# Revit family: НЕВАТОМ_Neiva 2 подвесная С-W-R 3000, Версия 2
name_source: partatom
category: Оборудование
revit_build: Autodesk Revit 2017 (Build: 20170118_1100(x64)
units: mm (PartAtom-declared; Revit-internal decimal feet)

## family parameters
Всегда вертикально = Нет
На основе рабочей плоскости = Да
Общий = Нет
При загрузке вырезать с полостями = Нет
Размер круглого соединителя = Использовать диаметр
Тип детали = Нормальный
Точка расчета площади = Нет

## types (1)
- C-3000-W-R
    A1 = 830 мм
    ADSK_Единица измерения = шт.
    ADSK_Завод-изготовитель = НЕВАТОМ
    ADSK_Количество = 1
    ADSK_Количество фаз = 3
    ADSK_Коэффициент мощности = 0.8
    ADSK_Марка = C-3000-W-R
    ADSK_Масса = 90
    ADSK_Материал наименование = сталь оцинкованная крашенная
    ADSK_Наименование = C-3000-W-R
    ADSK_Напряжение = 400 В
    ADSK_Номинальная мощность = 1140 Вт
    ADSK_Полная мощность = 1425 В·А
    ADSK_Потеря давления воздуха = 0.0 Па
    ADSK_Размер_Высота = 510 мм
    ADSK_Размер_Длина = 1218 мм
    ADSK_Размер_Ширина = 860 мм
    ADSK_Расход воздуха = 0.0 м³/ч
    ADSK_Температура воздуха на входе в нагреватель = 90 °C
    ADSK_Ток = 2 А
    Nevatom_Мощность нагревателя = 0 Вт
    Nevatom_Напорная характеристика, P = 0.0 Па
    Nevatom_Напорная характеристика, Р1 = 200.0 Па
    PG = 0 мм
    a влево = 578 мм
    b вверх = 80 мм
    b1 = 272 мм
    b2 = 174 мм
    b3 = 126 мм
    b4 = 75 мм
    c низ влево = 620 мм
    d вниз = 60 мм
    f1 = 40 мм
    f2 = 45 мм
    f3 = 45 мм
    f4 = 64 мм
    f5 = 65 мм
    f6 = 25 мм
    g1 = 18 мм
    g3 = 130 мм
    g4 = 75 мм
    g5 = 240 мм
    g6 = 200 мм
    k  длина = 313 мм
    m = 38 мм
    s = 17 мм
    А6 = 450 мм
    НЕВАТОМ_Температура воды на выходе из нагревателя = 70 °C
    Отметка по умолчанию = 0 мм
    Питание, В = 220
    вводный канал b = 68 мм
    вводный канал d = 255 мм
    вводный канал а = 946 мм
    вводный канал с = 945 мм
    высота ПВУ = 510 мм
    высота щита = 360 мм
    глубина ПВУ = 860 мм
    глубина щита = 100 мм
    длина ПВУ = 1218 мм
    длина щита = 440 мм
    п1 = 128 мм
    п2 = 178 мм
    п3 = 230 мм
    п4 = 418 мм
    п5 = 468 мм
    расстояние до щита = 0 мм
    расстояние справа от щита = 592 мм
